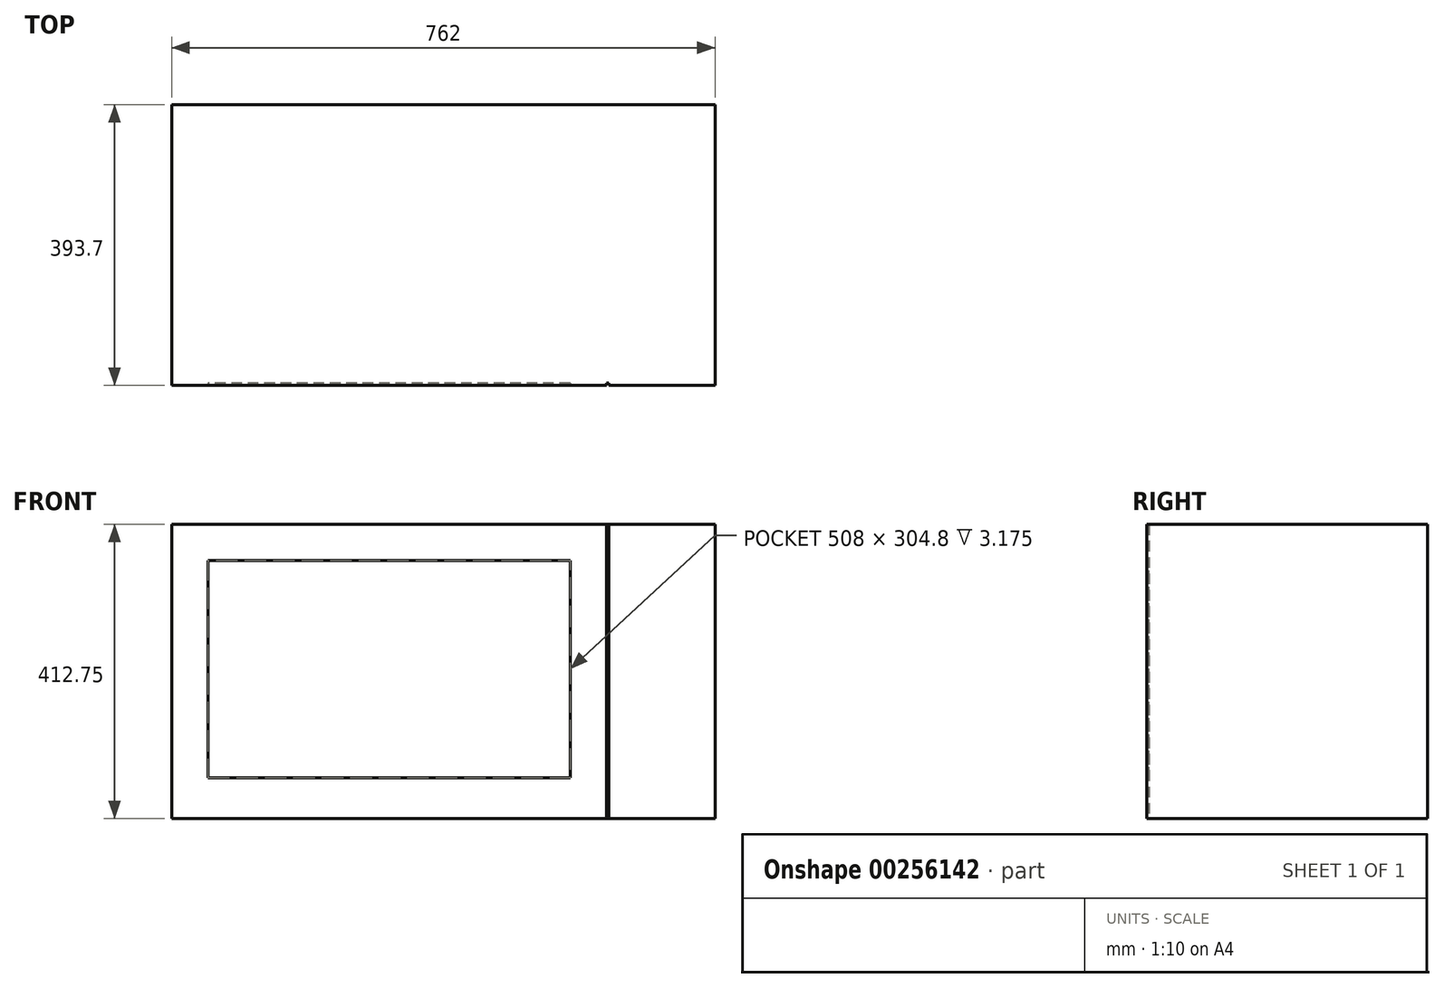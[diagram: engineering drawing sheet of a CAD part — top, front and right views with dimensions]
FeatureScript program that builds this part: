
annotation { "Feature Type Name" : "Feature", "Feature Type Description" : "" }
export const myFeature = defineFeature(function(context is Context, id is Id, definition is map)
    precondition{}
    {
        {
            var Q0;
            Q0=qCreatedBy(makeId("Right.planeOp"),FACE);
            var sketch = newSketch(context, id + "F0", { "sketchPlane" : qUnion([Q0])});
            skLineSegment(sketch, "E0", {"start": v(0, 0) * mm, "end": v(0, 412.75) * mm});
            skLineSegment(sketch, "E1", {"start": v(0, 0) * mm, "end": v(-393.7, 0) * mm});
            skLineSegment(sketch, "E2", {"start": v(-393.7, 0) * mm, "end": v(-393.7, 412.75) * mm});
            skLineSegment(sketch, "E3", {"start": v(-393.7, 412.75) * mm, "end": v(0, 412.75) * mm});
            skSolve(sketch);
        }
        {
            var Q0;
            Q0=makeQuery(id+"F0.imprint","IMPRINT",FACE,{"disambiguationData":[TD([[makeQuery(id+"F0.imprint","IMPRINT",EDGE,{"derivedFrom":sQuery(id+"F0.wireOp",EDGE,"E0")}),1.0]])]});
            extrude(context, id + "F1", {"entities" : qUnion([Q0]), "endBound" : BoundingType.SYMMETRIC, "depth" : 762 * mm});
        }
        {
            var Q0;
            Q0=makeQuery(id+"F1.opExtrude","SWEPT_FACE",FACE,{"disambiguationData":[OSD([sQuery(id+"F0.wireOp",EDGE,"E2")])]});
            var sketch = newSketch(context, id + "F2", { "sketchPlane" : qUnion([Q0])});
            skLineSegment(sketch, "E4.bottom", {"start": v(177.8, 57.15) * mm, "end": v(-330.2, 57.15) * mm});
            skLineSegment(sketch, "E4.top", {"start": v(177.8, 361.95) * mm, "end": v(-330.2, 361.95) * mm});
            skLineSegment(sketch, "E4.left", {"start": v(177.8, 57.15) * mm, "end": v(177.8, 361.95) * mm});
            skLineSegment(sketch, "E4.right", {"start": v(-330.2, 57.15) * mm, "end": v(-330.2, 361.95) * mm});
            skPoint(sketch, "E4.middle", {"position": v(0, 209.55) * mm});
            skSolve(sketch);
        }
        {
            var Q0;
            Q0=qSketchRegion(id+"F2",true);
            extrude(context, id + "F3", {"entities" : qUnion([Q0]), "operationType" : NewBodyOperationType.REMOVE, "oppositeDirection" : true, "depth" : 3.17 * mm});
        }
        {
            var Q0;
            Q0=makeQuery(id+"F1.opExtrude","SWEPT_FACE",FACE,{"disambiguationData":[OSD([sQuery(id+"F0.wireOp",EDGE,"E2")])]});
            var sketch = newSketch(context, id + "F4", { "sketchPlane" : qUnion([Q0])});
            skLineSegment(sketch, "E5.bottom", {"start": v(228.6, 483.75) * mm, "end": v(231.8, 483.75) * mm});
            skLineSegment(sketch, "E5.top", {"start": v(228.6, -79.73) * mm, "end": v(231.8, -79.73) * mm});
            skLineSegment(sketch, "E5.left", {"start": v(228.6, 483.75) * mm, "end": v(228.6, -79.73) * mm});
            skLineSegment(sketch, "E5.right", {"start": v(231.8, 483.75) * mm, "end": v(231.8, -79.73) * mm});
            skSolve(sketch);
        }
        {
            var Q0;
            Q0=qSketchRegion(id+"F4",true);
            extrude(context, id + "F5", {"entities" : qUnion([Q0]), "operationType" : NewBodyOperationType.REMOVE, "oppositeDirection" : true, "depth" : 3.17 * mm});
        }
    });
